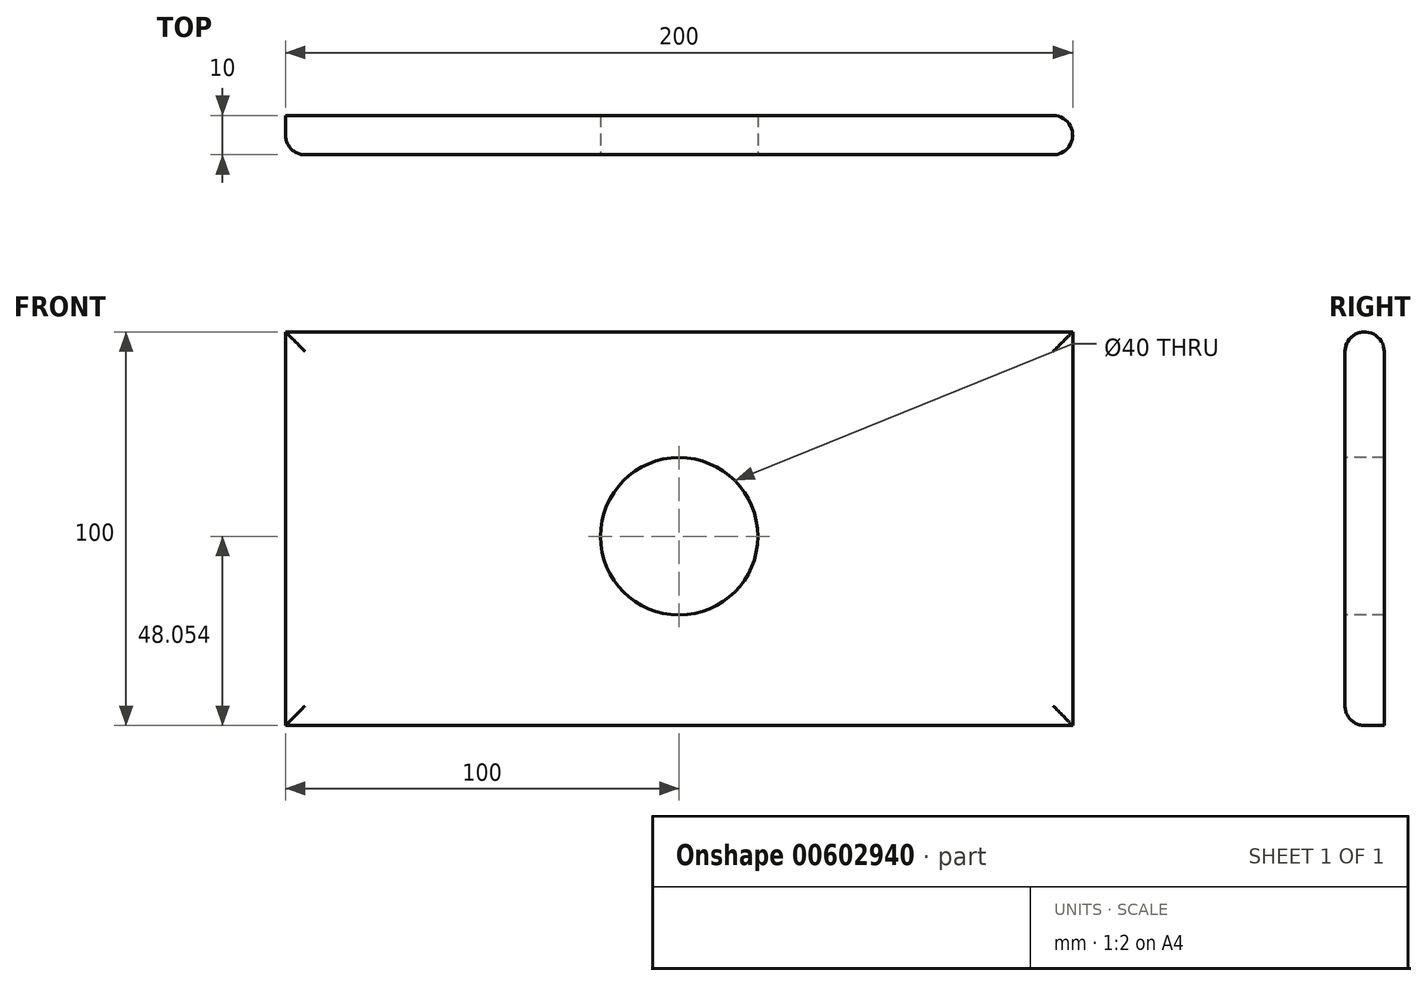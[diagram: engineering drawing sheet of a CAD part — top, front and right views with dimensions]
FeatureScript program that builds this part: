
annotation { "Feature Type Name" : "Feature", "Feature Type Description" : "" }
export const myFeature = defineFeature(function(context is Context, id is Id, definition is map)
    precondition{}
    {
        {
            var Q0;
            Q0=qCreatedBy(makeId("Front.planeOp"),FACE);
            var sketch = newSketch(context, id + "F0", { "sketchPlane" : qUnion([Q0])});
            skLineSegment(sketch, "E0.bottom", {"start": v(-100, 50) * mm, "end": v(100, 50) * mm});
            skLineSegment(sketch, "E0.top", {"start": v(-100, -50) * mm, "end": v(100, -50) * mm});
            skLineSegment(sketch, "E0.left", {"start": v(-100, 50) * mm, "end": v(-100, -50) * mm});
            skLineSegment(sketch, "E0.right", {"start": v(100, 50) * mm, "end": v(100, -50) * mm});
            skPoint(sketch, "E0.middle", {"position": v(0, 0) * mm});
            skSolve(sketch);
        }
        {
            var Q0;
            Q0 = qSketchRegion(id + "F0", true);
            extrude(context, id + "F1", {"entities" : qUnion([Q0]), "depth" : 10 * mm, "offsetDistance" : 25 * mm});
        }
        {
            var Q0;
            Q0=makeQuery(id+"F1.opExtrude","CAP_FACE",FACE,{"disambiguationData":[OSD([sQuery(id+"F0.wireOp",EDGE,"E0.bottom"),sQuery(id+"F0.wireOp",EDGE,"E0.top"),sQuery(id+"F0.wireOp",EDGE,"E0.left"),sQuery(id+"F0.wireOp",EDGE,"E0.right")])],"isStart":false});
            var sketch = newSketch(context, id + "F2", { "sketchPlane" : qUnion([Q0])});
            skCircle(sketch, "E1", {"center": v(0, -1.95) * mm, "radius": 20 * mm});
            skSolve(sketch);
        }
        {
            var Q0;
            Q0 = qSketchRegion(id + "F2", true);
            extrude(context, id + "F3", {"entities" : qUnion([Q0]), "operationType" : NewBodyOperationType.REMOVE, "endBound" : BoundingType.THROUGH_ALL, "oppositeDirection" : true, "depth" : 25 * mm, "offsetDistance" : 25 * mm});
        }
        {
            var Q0;
            Q0=makeQuery(id+"F1.opExtrude","CAP_EDGE",EDGE,{"disambiguationData":[OSD([sQuery(id+"F0.wireOp",EDGE,"E0.bottom")])],"isStart":false});
            var Q1;
            Q1=makeQuery(id+"F1.opExtrude","CAP_EDGE",EDGE,{"disambiguationData":[OSD([sQuery(id+"F0.wireOp",EDGE,"E0.bottom")])],"isStart":true});
            var Q2;
            Q2=makeQuery(id+"F1.opExtrude","CAP_EDGE",EDGE,{"disambiguationData":[OSD([sQuery(id+"F0.wireOp",EDGE,"E0.right")])],"isStart":true});
            var Q3;
            Q3=makeQuery(id+"F1.opExtrude","CAP_EDGE",EDGE,{"disambiguationData":[OSD([sQuery(id+"F0.wireOp",EDGE,"E0.right")])],"isStart":false});
            var Q4;
            Q4=makeQuery(id+"F1.opExtrude","CAP_EDGE",EDGE,{"disambiguationData":[OSD([sQuery(id+"F0.wireOp",EDGE,"E0.top")])],"isStart":false});
            var Q5;
            Q5=makeQuery(id+"F1.opExtrude","CAP_EDGE",EDGE,{"disambiguationData":[OSD([sQuery(id+"F0.wireOp",EDGE,"E0.left")])],"isStart":false});
            fillet(context, id + "F4", {"entities" : qUnion([Q0, Q1, Q2, Q3, Q4, Q5]), "radius" : 5 * mm, "tangentPropagation" : true, "allowEdgeOverflow" : false});
        }
    });
